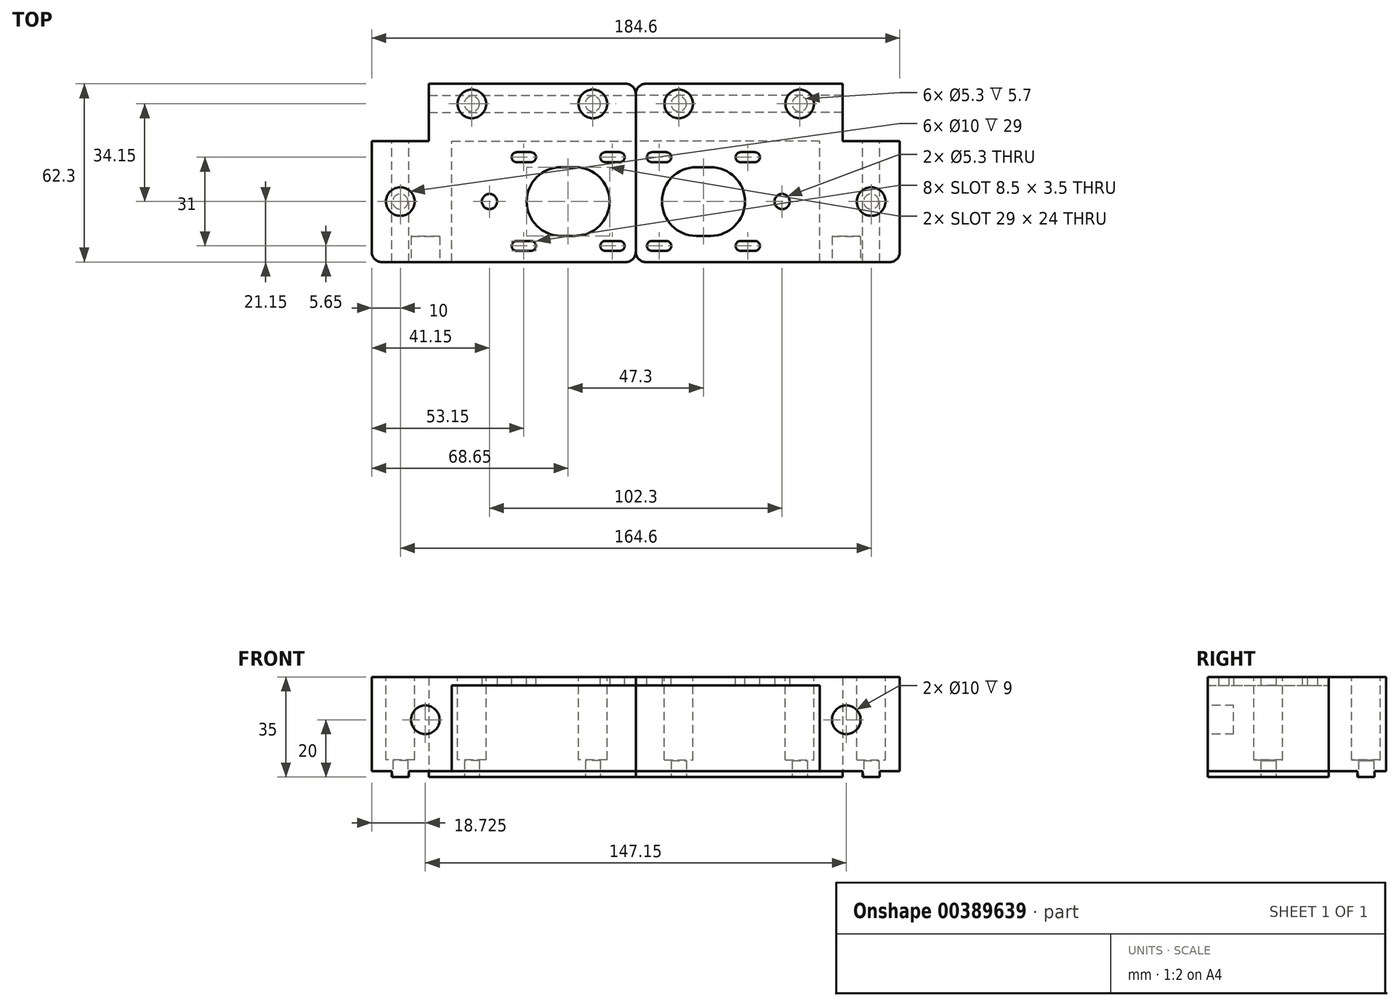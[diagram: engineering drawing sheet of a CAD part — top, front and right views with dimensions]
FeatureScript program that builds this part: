
annotation { "Feature Type Name" : "Feature", "Feature Type Description" : "" }
export const myFeature = defineFeature(function(context is Context, id is Id, definition is map)
    precondition{}
    {
        {
            var Q0;
            Q0=qCreatedBy(makeId("Top.planeOp"),FACE);
            var sketch = newSketch(context, id + "F0", { "sketchPlane" : qUnion([Q0])});
            skLineSegment(sketch, "E0", {"start": v(-21.15, 41.15) * mm, "end": v(8.85, 41.15) * mm});
            skCircle(sketch, "E1", {"center": v(0, 0) * mm, "radius": 2.65 * mm});
            skCircle(sketch, "E2", {"center": v(-31.15, 0) * mm, "radius": 2.65 * mm});
            skCircle(sketch, "E3", {"center": v(-6.15, 34.15) * mm, "radius": 2.65 * mm});
            skPoint(sketch, "E3.centerSnap0", {"position": v(-6.15, 41.15) * mm});
            skPoint(sketch, "E3.centerSnap1", {"position": v(-27.3, 34.15) * mm});
            skLineSegment(sketch, "E4.left", {"start": v(-41.15, 21.15) * mm, "end": v(-41.15, -21.15) * mm});
            skLineSegment(sketch, "E4.right", {"start": v(8.85, 41.15) * mm, "end": v(8.85, -21.15) * mm});
            skLineSegment(sketch, "E5", {"start": v(-41.15, -21.15) * mm, "end": v(8.85, -21.15) * mm});
            skPoint(sketch, "E6.orphan", {"position": v(8.85, 24.15) * mm});
            skLineSegment(sketch, "E7", {"start": v(-41.15, 21.15) * mm, "end": v(-21.15, 21.15) * mm});
            skLineSegment(sketch, "E8", {"start": v(-21.15, 21.15) * mm, "end": v(-21.15, 41.15) * mm});
            skLineSegment(sketch, "E9.bottom", {"start": v(8.85, -21.15) * mm, "end": v(51.15, -21.15) * mm});
            skLineSegment(sketch, "E9.top", {"start": v(8.85, 41.15) * mm, "end": v(51.15, 41.15) * mm});
            skLineSegment(sketch, "E9.left", {"start": v(8.85, -21.15) * mm, "end": v(8.85, 41.15) * mm});
            skLineSegment(sketch, "E9.right", {"start": v(51.15, -21.15) * mm, "end": v(51.15, 41.15) * mm});
            skCircle(sketch, "E10", {"center": v(30, 0) * mm, "radius": 12 * mm});
            skCircle(sketch, "E11", {"center": v(36.15, 34.15) * mm, "radius": 2.65 * mm});
            skSolve(sketch);
        }
        {
            var Q0;
            Q0=qSketchRegion(id+"F0",true);
            extrude(context, id + "F1", {"entities" : qUnion([Q0]), "depth" : 33 * mm});
        }
        {
            var Q0;
            Q0=makeQuery(id+"F1.opExtrude","SWEPT_FACE",FACE,{"disambiguationData":[OSD([sQuery(id+"F0.wireOp",EDGE,"E5")])]});
            var sketch = newSketch(context, id + "F2", { "sketchPlane" : qUnion([Q0])});
            skCircle(sketch, "E12", {"center": v(-22.43, 18) * mm, "radius": 5 * mm});
            skSolve(sketch);
        }
        {
            var Q0;
            Q0=qSketchRegion(id+"F2",true);
            extrude(context, id + "F3", {"entities" : qUnion([Q0]), "operationType" : NewBodyOperationType.REMOVE, "oppositeDirection" : true, "depth" : 9 * mm});
        }
        {
            var Q0;
            Q0=makeQuery(id+"F0.imprint","IMPRINT",FACE,{"disambiguationData":[TD([[makeQuery(id+"F0.imprint","IMPRINT",EDGE,{"derivedFrom":sQuery(id+"F0.wireOp",EDGE,"E0")}),-1.0]])]});
            var sketch = newSketch(context, id + "F4", { "sketchPlane" : qUnion([Q0])});
            skLineSegment(sketch, "E13.left", {"start": v(-13.15, -21.15) * mm, "end": v(-13.15, 21.15) * mm});
            skLineSegment(sketch, "E14.bottom", {"start": v(-13.15, -21.15) * mm, "end": v(51.15, -21.15) * mm});
            skLineSegment(sketch, "E14.top", {"start": v(-13.15, 21.15) * mm, "end": v(51.15, 21.15) * mm});
            skLineSegment(sketch, "E14.right", {"start": v(51.15, -21.15) * mm, "end": v(51.15, 21.15) * mm});
            skSolve(sketch);
        }
        {
            var Q0;
            Q0=qSketchRegion(id+"F4",true);
            extrude(context, id + "F5", {"entities" : qUnion([Q0]), "operationType" : NewBodyOperationType.REMOVE, "depth" : 30 * mm});
        }
        {
            var Q0;
            Q0=makeQuery(id+"F1.opExtrude","CAP_FACE",FACE,{"disambiguationData":[OSD([sQuery(id+"F0.wireOp",EDGE,"E0"),sQuery(id+"F0.wireOp",EDGE,"E1"),sQuery(id+"F0.wireOp",EDGE,"E2"),sQuery(id+"F0.wireOp",EDGE,"E3"),sQuery(id+"F0.wireOp",EDGE,"E4.left"),sQuery(id+"F0.wireOp",EDGE,"E4.right"),sQuery(id+"F0.wireOp",EDGE,"33121b06-638f-45b1-bab2-25962b6da09b"),sQuery(id+"F0.wireOp",EDGE,"E5"),sQuery(id+"F0.wireOp",EDGE,"E7"),sQuery(id+"F0.wireOp",EDGE,"E8")])],"isStart":false});
            var sketch = newSketch(context, id + "F6", { "sketchPlane" : qUnion([Q0])});
            skPoint(sketch, "E15.0", {"position": v(-6.15, 34.15) * mm});
            skPoint(sketch, "E15.1", {"position": v(-31.15, 0) * mm});
            skCircle(sketch, "E16", {"center": v(-6.15, 34.15) * mm, "radius": 5 * mm});
            skCircle(sketch, "E17", {"center": v(-31.15, 0) * mm, "radius": 5 * mm});
            skPoint(sketch, "E18", {"position": v(36.15, 34.15) * mm});
            skPoint(sketch, "E19", {"position": v(0, 0) * mm});
            skCircle(sketch, "E20", {"center": v(36.15, 34.15) * mm, "radius": 5 * mm});
            skSolve(sketch);
        }
        {
            var Q0;
            Q0=qSketchRegion(id+"F6",true);
            extrude(context, id + "F7", {"entities" : qUnion([Q0]), "operationType" : NewBodyOperationType.REMOVE, "oppositeDirection" : true, "depth" : 29 * mm});
        }
        {
            var Q0;
            Q0=makeQuery(id+"F0.imprint","IMPRINT",FACE,{"disambiguationData":[TD([[makeQuery(id+"F0.imprint","IMPRINT",EDGE,{"derivedFrom":sQuery(id+"F0.wireOp",EDGE,"E0")}),-1.0]])]});
            var sketch = newSketch(context, id + "F8", { "sketchPlane" : qUnion([Q0])});
            skLineSegment(sketch, "E21.bottom", {"start": v(-34.1, -21.15) * mm, "end": v(-28.2, -21.15) * mm});
            skLineSegment(sketch, "E21.top", {"start": v(-34.1, 21.15) * mm, "end": v(-28.2, 21.15) * mm});
            skLineSegment(sketch, "E21.left", {"start": v(-34.1, -21.15) * mm, "end": v(-34.1, 21.15) * mm});
            skLineSegment(sketch, "E21.right", {"start": v(-28.2, -21.15) * mm, "end": v(-28.2, 21.15) * mm});
            skLineSegment(sketch, "E22.bottom", {"start": v(-21.15, 31.2) * mm, "end": v(51.15, 31.2) * mm});
            skLineSegment(sketch, "E22.top", {"start": v(-21.15, 37.1) * mm, "end": v(51.15, 37.1) * mm});
            skLineSegment(sketch, "E22.left", {"start": v(-21.15, 31.2) * mm, "end": v(-21.15, 37.1) * mm});
            skLineSegment(sketch, "E22.right", {"start": v(51.15, 31.2) * mm, "end": v(51.15, 37.1) * mm});
            skCircle(sketch, "E23.0", {"center": v(-31.15, 0) * mm, "radius": 2.65 * mm});
            skCircle(sketch, "E24.0", {"center": v(-6.15, 34.15) * mm, "radius": 2.65 * mm});
            skCircle(sketch, "E25.0", {"center": v(36.15, 34.15) * mm, "radius": 2.65 * mm});
            skSolve(sketch);
        }
        {
            var Q0;
            Q0=qSketchRegion(id+"F8",true);
            extrude(context, id + "F9", {"entities" : qUnion([Q0]), "operationType" : NewBodyOperationType.ADD, "oppositeDirection" : true, "depth" : 2 * mm});
        }
        {
            var Q0;
            Q0=makeQuery(id+"F1.opExtrude","CAP_FACE",FACE,{"disambiguationData":[OSD([sQuery(id+"F0.wireOp",EDGE,"E0"),sQuery(id+"F0.wireOp",EDGE,"E1"),sQuery(id+"F0.wireOp",EDGE,"E2"),sQuery(id+"F0.wireOp",EDGE,"E3"),sQuery(id+"F0.wireOp",EDGE,"E4.left"),sQuery(id+"F0.wireOp",EDGE,"E4.right"),sQuery(id+"F0.wireOp",EDGE,"33121b06-638f-45b1-bab2-25962b6da09b"),sQuery(id+"F0.wireOp",EDGE,"E5"),sQuery(id+"F0.wireOp",EDGE,"E7"),sQuery(id+"F0.wireOp",EDGE,"E8")])],"isStart":false});
            var sketch = newSketch(context, id + "F10", { "sketchPlane" : qUnion([Q0])});
            skLineSegment(sketch, "E26.bottom", {"start": v(14.5, 15.5) * mm, "end": v(45.5, 15.5) * mm, "construction": true});
            skLineSegment(sketch, "E26.top", {"start": v(14.5, -15.5) * mm, "end": v(45.5, -15.5) * mm, "construction": true});
            skLineSegment(sketch, "E26.left", {"start": v(14.5, 15.5) * mm, "end": v(14.5, -15.5) * mm, "construction": true});
            skLineSegment(sketch, "E26.right", {"start": v(45.5, 15.5) * mm, "end": v(45.5, -15.5) * mm, "construction": true});
            skCircle(sketch, "E27.converted", {"center": v(45.5, 15.5) * mm, "radius": 1.75 * mm});
            skCircle(sketch, "E28.converted", {"center": v(14.5, 15.5) * mm, "radius": 1.75 * mm});
            skCircle(sketch, "E29.converted", {"center": v(14.5, -15.5) * mm, "radius": 1.75 * mm});
            skCircle(sketch, "E30.converted", {"center": v(45.5, -15.5) * mm, "radius": 1.75 * mm});
            skPoint(sketch, "E31", {"position": v(30, 0) * mm});
            skCircle(sketch, "E32", {"center": v(9.5, -15.5) * mm, "radius": 1.75 * mm});
            skCircle(sketch, "E33", {"center": v(9.5, 15.5) * mm, "radius": 1.75 * mm});
            skCircle(sketch, "E34", {"center": v(40.5, 15.5) * mm, "radius": 1.75 * mm});
            skCircle(sketch, "E35", {"center": v(40.5, -15.5) * mm, "radius": 1.75 * mm});
            skCircle(sketch, "E36", {"center": v(25, 0) * mm, "radius": 12 * mm});
            skLineSegment(sketch, "E37", {"start": v(9.5, -17.25) * mm, "end": v(14.5, -17.25) * mm});
            skLineSegment(sketch, "E38", {"start": v(9.5, -13.75) * mm, "end": v(14.5, -13.75) * mm});
            skLineSegment(sketch, "E39", {"start": v(40.5, -17.25) * mm, "end": v(45.5, -17.25) * mm});
            skLineSegment(sketch, "E40", {"start": v(40.5, -13.75) * mm, "end": v(45.5, -13.75) * mm});
            skLineSegment(sketch, "E41", {"start": v(9.5, 13.75) * mm, "end": v(14.5, 13.75) * mm});
            skLineSegment(sketch, "E42", {"start": v(9.5, 17.25) * mm, "end": v(14.5, 17.25) * mm});
            skLineSegment(sketch, "E43", {"start": v(40.5, 13.75) * mm, "end": v(45.5, 13.75) * mm});
            skLineSegment(sketch, "E44", {"start": v(40.5, 17.25) * mm, "end": v(45.5, 17.25) * mm});
            skLineSegment(sketch, "E45", {"start": v(25, 12) * mm, "end": v(30, 12) * mm});
            skLineSegment(sketch, "E46", {"start": v(25, -12) * mm, "end": v(30, -12) * mm});
            skCircle(sketch, "E47.0", {"center": v(30, 0) * mm, "radius": 12 * mm});
            skSolve(sketch);
        }
        {
            var Q0;
            Q0=qSketchRegion(id+"F10",true);
            extrude(context, id + "F11", {"entities" : qUnion([Q0]), "operationType" : NewBodyOperationType.REMOVE, "endBound" : BoundingType.THROUGH_ALL, "oppositeDirection" : true, "depth" : 25 * mm});
        }
        {
            var Q0;
            Q0=makeQuery(id+"F7.boolean.opBoolean","COPY",FACE,{"derivedFrom":makeQuery(id+"F7.opExtrude","CAP_FACE",FACE,{"disambiguationData":[OSD([sQuery(id+"F6.wireOp",EDGE,"E17")])],"isStart":false})});
            var sketch = newSketch(context, id + "F12", { "sketchPlane" : qUnion([Q0])});
            skCircle(sketch, "E48.0", {"center": v(-31.15, 0) * mm, "radius": 2.65 * mm});
            skCircle(sketch, "E49.0", {"center": v(-6.15, 34.15) * mm, "radius": 2.65 * mm});
            skCircle(sketch, "E50.0", {"center": v(36.15, 34.15) * mm, "radius": 2.65 * mm});
            skSolve(sketch);
        }
        {
            var Q0;
            Q0=qSketchRegion(id+"F12",true);
            extrude(context, id + "F13", {"entities" : qUnion([Q0]), "operationType" : NewBodyOperationType.ADD, "oppositeDirection" : true, "depth" : .3 * mm});
        }
        {
            var Q0;
            Q0=makeQuery(id+"F1.opExtrude","SWEPT_EDGE",EDGE,{"disambiguationData":[OSD([sQuery(id+"F0.wireOp",EDGE,"E4.left"),sQuery(id+"F0.wireOp",EDGE,"E5")])]});
            var Q1;
            Q1=makeQuery(id+"F1.opExtrude","SWEPT_EDGE",EDGE,{"disambiguationData":[OSD([sQuery(id+"F0.wireOp",EDGE,"E9.bottom"),sQuery(id+"F0.wireOp",EDGE,"E9.right")])]});
            var Q2;
            Q2=makeQuery(id+"F1.opExtrude","SWEPT_EDGE",EDGE,{"disambiguationData":[OSD([sQuery(id+"F0.wireOp",EDGE,"E9.top"),sQuery(id+"F0.wireOp",EDGE,"E9.right")])]});
            fillet(context, id + "F14", {"entities" : qUnion([Q0, Q1, Q2]), "radius" : 3.5 * mm, "tangentPropagation" : true, "allowEdgeOverflow" : false});
        }
        {
            var Q0;
            Q0=makeQuery(id+"F1.opExtrude","SWEPT_BODY",BODY,{"disambiguationData":[OSD([sQuery(id+"F0.wireOp",EDGE,"E0"),sQuery(id+"F0.wireOp",EDGE,"E1"),sQuery(id+"F0.wireOp",EDGE,"E2"),sQuery(id+"F0.wireOp",EDGE,"E3"),sQuery(id+"F0.wireOp",EDGE,"E4.left"),sQuery(id+"F0.wireOp",EDGE,"33121b06-638f-45b1-bab2-25962b6da09b"),sQuery(id+"F0.wireOp",EDGE,"E5"),sQuery(id+"F0.wireOp",EDGE,"E7"),sQuery(id+"F0.wireOp",EDGE,"E8"),sQuery(id+"F0.wireOp",EDGE,"E9.bottom"),sQuery(id+"F0.wireOp",EDGE,"E9.top"),sQuery(id+"F0.wireOp",EDGE,"E9.right"),sQuery(id+"F0.wireOp",EDGE,"E10"),sQuery(id+"F0.wireOp",EDGE,"E11")])]});
            var Q1;
            Q1=makeQuery(id+"F9.boolean.opBoolean","MERGE",FACE,{"derivedFrom":[makeQuery(id+"F1.opExtrude","SWEPT_FACE",FACE,{"disambiguationData":[OSD([sQuery(id+"F0.wireOp",EDGE,"E9.right")])]}),makeQuery(id+"F9.opExtrude","SWEPT_FACE",FACE,{"disambiguationData":[OSD([sQuery(id+"F8.wireOp",EDGE,"E22.right")])]})]});
            mirror(context, id + "F15", {"entities" : qUnion([Q0]), "mirrorPlane" : qUnion([Q1])});
        }
    });
